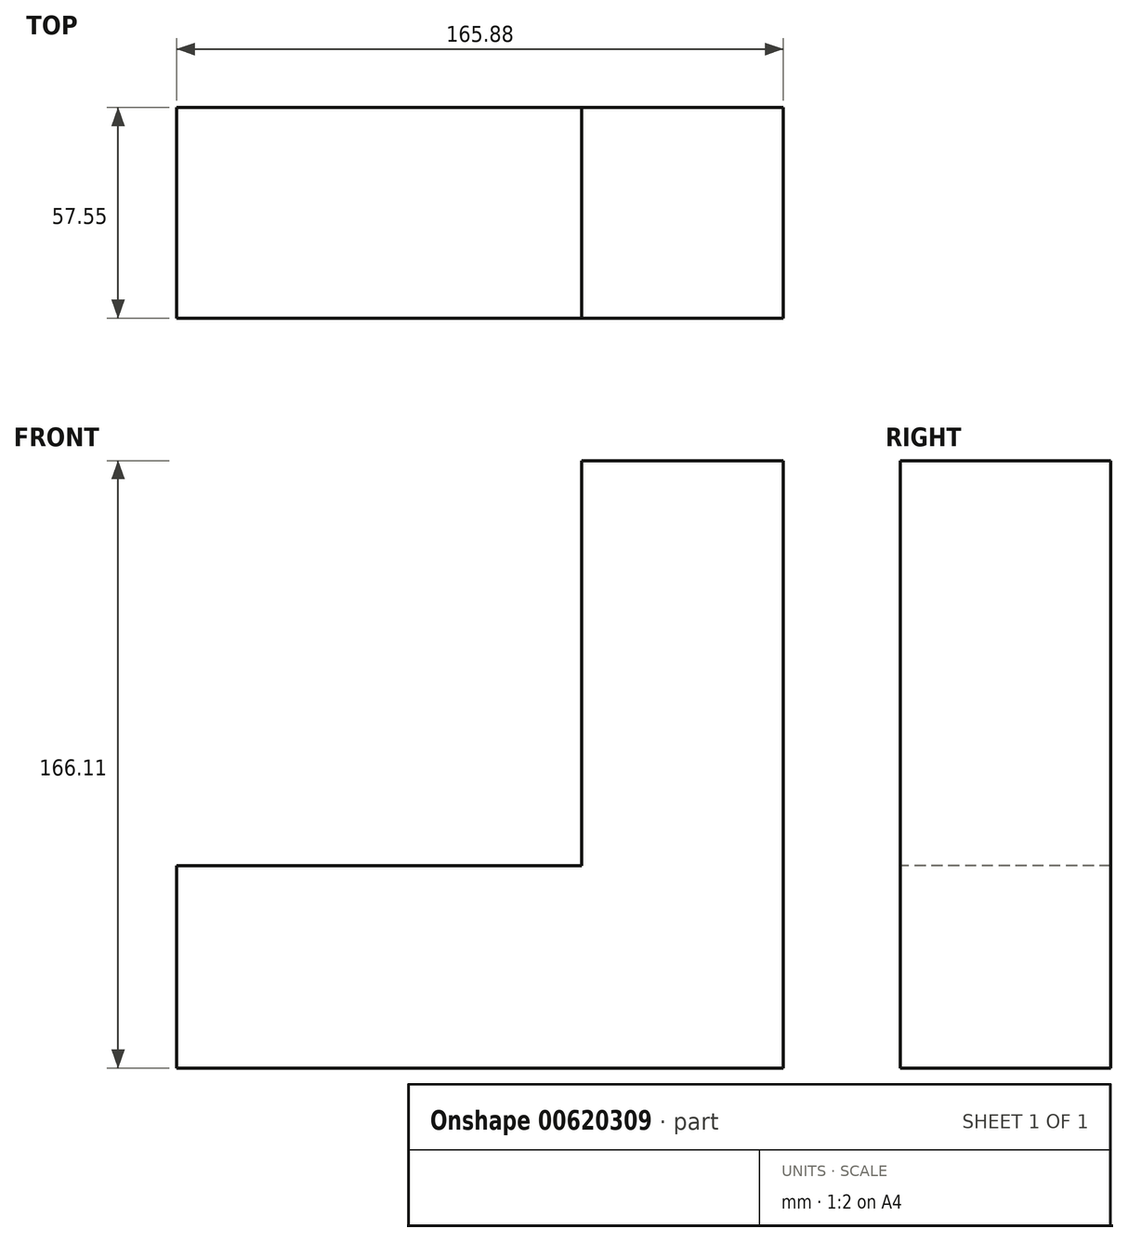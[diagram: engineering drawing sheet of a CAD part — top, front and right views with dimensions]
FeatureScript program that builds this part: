
annotation { "Feature Type Name" : "Feature", "Feature Type Description" : "" }
export const myFeature = defineFeature(function(context is Context, id is Id, definition is map)
    precondition{}
    {
        {
            var Q0;
            Q0=qCreatedBy(makeId("Top.planeOp"),FACE);
            var sketch = newSketch(context, id + "F0", { "sketchPlane" : qUnion([Q0])});
            skLineSegment(sketch, "E0.bottom", {"start": v(0, 0) * mm, "end": v(55.14, 0) * mm});
            skLineSegment(sketch, "E0.top", {"start": v(0, -57.55) * mm, "end": v(55.14, -57.55) * mm});
            skLineSegment(sketch, "E0.left", {"start": v(0, 0) * mm, "end": v(0, -57.55) * mm});
            skLineSegment(sketch, "E0.right", {"start": v(55.14, 0) * mm, "end": v(55.14, -57.55) * mm});
            skSolve(sketch);
        }
        {
            var Q0;
            Q0 = qSketchRegion(id + "F0", true);
            extrude(context, id + "F1", {"entities" : qUnion([Q0]), "depth" : 55.37 * mm, "offsetDistance" : 25.4 * mm});
        }
        {
            var Q0;
            Q0=makeQuery(id+"F1.opExtrude","CAP_FACE",FACE,{"disambiguationData":[OSD([sQuery(id+"F0.wireOp",EDGE,"E0.bottom"),sQuery(id+"F0.wireOp",EDGE,"E0.top"),sQuery(id+"F0.wireOp",EDGE,"E0.left"),sQuery(id+"F0.wireOp",EDGE,"E0.right")])],"isStart":false});
            var sketch = newSketch(context, id + "F2", { "sketchPlane" : qUnion([Q0])});
            skLineSegment(sketch, "E1.bottom", {"start": v(0, -57.55) * mm, "end": v(55.14, -57.55) * mm});
            skLineSegment(sketch, "E1.top", {"start": v(0, 0) * mm, "end": v(55.14, 0) * mm});
            skLineSegment(sketch, "E1.left", {"start": v(0, -57.55) * mm, "end": v(0, 0) * mm});
            skLineSegment(sketch, "E1.right", {"start": v(55.14, -57.55) * mm, "end": v(55.14, 0) * mm});
            skSolve(sketch);
        }
        {
            var Q0;
            Q0 = qSketchRegion(id + "F2", true);
            extrude(context, id + "F3", {"entities" : qUnion([Q0]), "operationType" : NewBodyOperationType.ADD, "depth" : 55.37 * mm, "offsetDistance" : 25.4 * mm});
        }
        {
            var Q0;
            Q0=makeQuery(id+"F1.opExtrude","CAP_FACE",FACE,{"disambiguationData":[OSD([sQuery(id+"F0.wireOp",EDGE,"E0.bottom"),sQuery(id+"F0.wireOp",EDGE,"E0.top"),sQuery(id+"F0.wireOp",EDGE,"E0.left"),sQuery(id+"F0.wireOp",EDGE,"E0.right")])],"isStart":true});
            var sketch = newSketch(context, id + "F4", { "sketchPlane" : qUnion([Q0])});
            skLineSegment(sketch, "E2.bottom", {"start": v(0, 57.55) * mm, "end": v(55.14, 57.55) * mm});
            skLineSegment(sketch, "E2.top", {"start": v(0, 0) * mm, "end": v(55.14, 0) * mm});
            skLineSegment(sketch, "E2.left", {"start": v(0, 57.55) * mm, "end": v(0, 0) * mm});
            skLineSegment(sketch, "E2.right", {"start": v(55.14, 57.55) * mm, "end": v(55.14, 0) * mm});
            skSolve(sketch);
        }
        {
            var Q0;
            Q0 = qSketchRegion(id + "F4", true);
            extrude(context, id + "F5", {"entities" : qUnion([Q0]), "operationType" : NewBodyOperationType.ADD, "depth" : 55.37 * mm, "offsetDistance" : 25.4 * mm});
        }
        {
            var Q0;
            Q0=makeQuery(id+"F5.boolean.opBoolean","MERGE",FACE,{"derivedFrom":[makeQuery(id+"F3.boolean.opBoolean","MERGE",FACE,{"derivedFrom":[makeQuery(id+"F1.opExtrude","SWEPT_FACE",FACE,{"disambiguationData":[OSD([sQuery(id+"F0.wireOp",EDGE,"E0.left")])]}),makeQuery(id+"F3.opExtrude","SWEPT_FACE",FACE,{"disambiguationData":[OSD([sQuery(id+"F2.wireOp",EDGE,"E1.left")])]})]}),makeQuery(id+"F5.opExtrude","SWEPT_FACE",FACE,{"disambiguationData":[OSD([sQuery(id+"F4.wireOp",EDGE,"E2.left")])]})]});
            var sketch = newSketch(context, id + "F6", { "sketchPlane" : qUnion([Q0])});
            skLineSegment(sketch, "E3.bottom", {"start": v(0, 0) * mm, "end": v(57.55, 0) * mm});
            skLineSegment(sketch, "E3.top", {"start": v(0, -55.37) * mm, "end": v(57.55, -55.37) * mm});
            skLineSegment(sketch, "E3.left", {"start": v(0, 0) * mm, "end": v(0, -55.37) * mm});
            skLineSegment(sketch, "E3.right", {"start": v(57.55, 0) * mm, "end": v(57.55, -55.37) * mm});
            skSolve(sketch);
        }
        {
            var Q0;
            Q0 = qSketchRegion(id + "F6", true);
            extrude(context, id + "F7", {"entities" : qUnion([Q0]), "operationType" : NewBodyOperationType.ADD, "depth" : 55.37 * mm, "offsetDistance" : 25.4 * mm});
        }
        {
            var Q0;
            Q0=makeQuery(id+"F7.opExtrude","CAP_FACE",FACE,{"disambiguationData":[OSD([sQuery(id+"F6.wireOp",EDGE,"E3.bottom"),sQuery(id+"F6.wireOp",EDGE,"E3.top"),sQuery(id+"F6.wireOp",EDGE,"E3.left"),sQuery(id+"F6.wireOp",EDGE,"E3.right")])],"isStart":false});
            var sketch = newSketch(context, id + "F8", { "sketchPlane" : qUnion([Q0])});
            skLineSegment(sketch, "E4.bottom", {"start": v(57.55, 0) * mm, "end": v(0, 0) * mm});
            skLineSegment(sketch, "E4.top", {"start": v(57.55, -55.37) * mm, "end": v(0, -55.37) * mm});
            skLineSegment(sketch, "E4.left", {"start": v(57.55, 0) * mm, "end": v(57.55, -55.37) * mm});
            skLineSegment(sketch, "E4.right", {"start": v(0, 0) * mm, "end": v(0, -55.37) * mm});
            skSolve(sketch);
        }
        {
            var Q0;
            Q0 = qSketchRegion(id + "F8", true);
            extrude(context, id + "F9", {"entities" : qUnion([Q0]), "operationType" : NewBodyOperationType.ADD, "depth" : 55.37 * mm, "offsetDistance" : 25.4 * mm});
        }
    });
